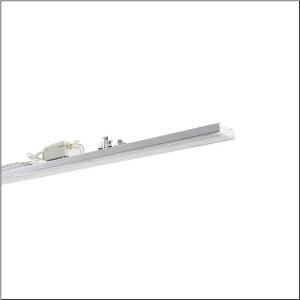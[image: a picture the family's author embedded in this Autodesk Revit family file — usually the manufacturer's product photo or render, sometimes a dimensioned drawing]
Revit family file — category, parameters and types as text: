
# Revit family: licross_r__21_recessed_mo_52tl1edv4e5g_66bd
name_source: partatom
category: Lighting Fixtures
units: mm (PartAtom-declared; Revit-internal decimal feet)

## family parameters
Cut with Voids When Loaded = No
Host = Face
Light Source = No
Part Type = Normal
Room Calculation Point = No
Round Connector Dimension = Use Diameter
Shared = No

## types (1)
- --- (1 x LED, 14910 lm, 85.3 W, 4000K)
    Apparent Load = 85 VA
    CIE Flux Codes = 85 95 99 100 100
    Color Rendering = 80
    Color Temperature = 4000K
    Default Elevation = 1800 mm
    Description = Licross® 21 Recessed MO, luminaire insert, of sheet steel, galvanised, coil coated, white, length: 2.250mm, width: 66mm, height: 67mm, LED rated luminous flux: 14.910lm, light colour: 840, control gear: DALI 2, with plug, 5-pole, with phase selection, mains connection: 220..240V, AC, 50/60Hz, rated input power: 85W, halogen-free wiring, primary light control with lens, of plastic, primary optical cover: cover, of PMMA, light emission: direct distribution, primary light characteristic: symmetric, protection rating (complete): IP40, insulation class (complete): insulation class I (protective earthing), certification: CE, ENEC, VDE, UKCA, protection symbol: D if used in an environment without relevant dust loads with corresponding accessories, impact resistance: IK06, permissible ambient temperature for indoor applications: -25..+35°C, corresponds to IFS (International Featured Standards) requirements for safety and quality in the food industry, reducing of maximum allowable ambient temperature of 5°C with ceiling mounting, LABS conformity tested according to VDMA 24364:2018-05, packaging unit: 1 piece
    Height = 58 mm
    Lamp = 1 x LED
    Lamp Light Flux = 14910 lm
    Lamp Power = 85.3 W
    Lamp count = 1
    Length = 2250 mm
    Luminous efficacy = 175 lm/W
    Manufacturer = Siteco
    ModVariant = No
    Model = 52TL1EDV4E5G
    Mounting Place = Ceiling
    Mounting Type = Pendant
    Number of Poles = 1
    OnlyDefault = Yes
    Power Factor = 1
    Product Name = Licross® 21 Recessed MO
    Product group = luminaire insert
    ProductGroupID = 901
    Protection Class = Protection class I
    Protection Degree = IP 40
    RLX_Detail_Level = 1
    RLX_Emergency_Light_Flux = 0 lm
    RLX_Emergency_Type = 0
    RLX_Emergency_Type_DB = No
    RlxData = <blob elided: 29761 chars, md5=0e5563d3>
    Socket = socket
    Standby Power = 0 W
    System Light Flux = 14910 lm
    System Power = 85 W
    Type Comments = factory setting: luminous flux: 100 % | dim-lin: 254 | 390 mA
    Type Image = l_1296930.jpg
    URL = http://relux.com
    VarID = @adj_057125
    Voltage = 0 V
    Weight = 0.00 kg
    Width = 66 mm

## geometry (parser evidence)
native form markers: Blend x4, Sweep x10
no freeform markers — native parametric forms only
